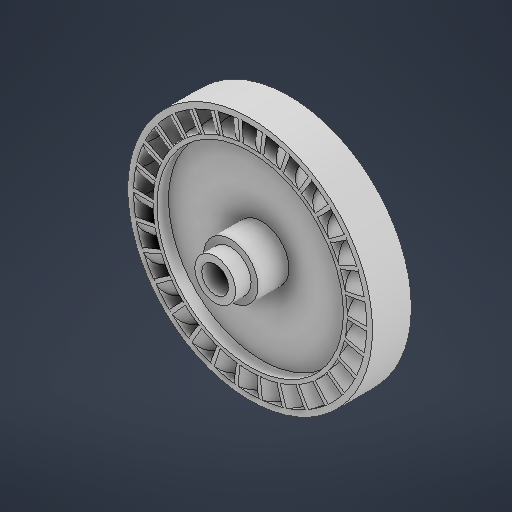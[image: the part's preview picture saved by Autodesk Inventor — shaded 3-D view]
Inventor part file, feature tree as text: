
AUTODESK INVENTOR PART (.ipt)
format: ipt  version: 2025.3 (Build 293356030, 356C)  size: 506,368 bytes
history: native  units: mm
features: extrude x7, sketch x5, projected_geometry x2, sweep x1, pattern_circular x1, fillet x1
ambient origin geometry x8: Origin, YZ Plane, XZ Plane, XY Plane, X Axis, Y Axis, Z Axis, Center Point
bodies: Solid1 (feature_tree)
feature tree (17):
  sketch  "Sketch1"  dims[d0=6.9mm d1=10.0mm]
  extrude  "Extrusion1"  Depth=10.0mm
  extrude  "Extrusion2"  Depth=48.0mm
  sweep  "Sweep1"
  extrude  "Extrusion3"  Depth=10.0mm TaperAngle=0.0deg
  pattern_circular  "Circular Pattern1"  [2 undecoded]
  extrude  "Extrusion4"  TaperAngle=0.0deg  [1 undecoded]
  extrude  "Extrusion5"  Depth=10.0mm TaperAngle=0.0deg
  fillet  "Fillet1"  Radius=300.0mm
  extrude  "Extrusion6"  Depth=7.0mm TaperAngle=0.0deg
  extrude  "Extrusion7"  Depth=4.0mm TaperAngle=0.0deg
  sketch  "Sketch2"  dims[d2=50.0mm d3=48.0mm]
  projected_geometry  "Projected Loop1"
  sketch  "Sketch3"  dims[d4=60.0mm d5=63.0mm]
  projected_geometry  "Projected Loop2"
  sketch  "Sketch4"  dims[d6=4.0mm d7=0.0mm d8=10.0mm d9=0.0mm]
  sketch  "Sketch5"  dims[d10=1.745329mm d11=1.0mm d12=0.0mm d13=0.0mm d14=10.0mm d15=0.0mm d16=300.0mm d17=360.0deg d19=7.0mm d20=0.0mm d21=1.0mm d22=0.0mm d23=3.0mm d24=14.0mm d25=12.0mm d26=0.0mm d27=10.5mm d28=4.0mm d29=0.0mm]
note: 3 required parameter values undecoded (feature->parameter linkage not recoverable at this tier; creation-order binding heuristic only, values carry confidence <= 0.55)
